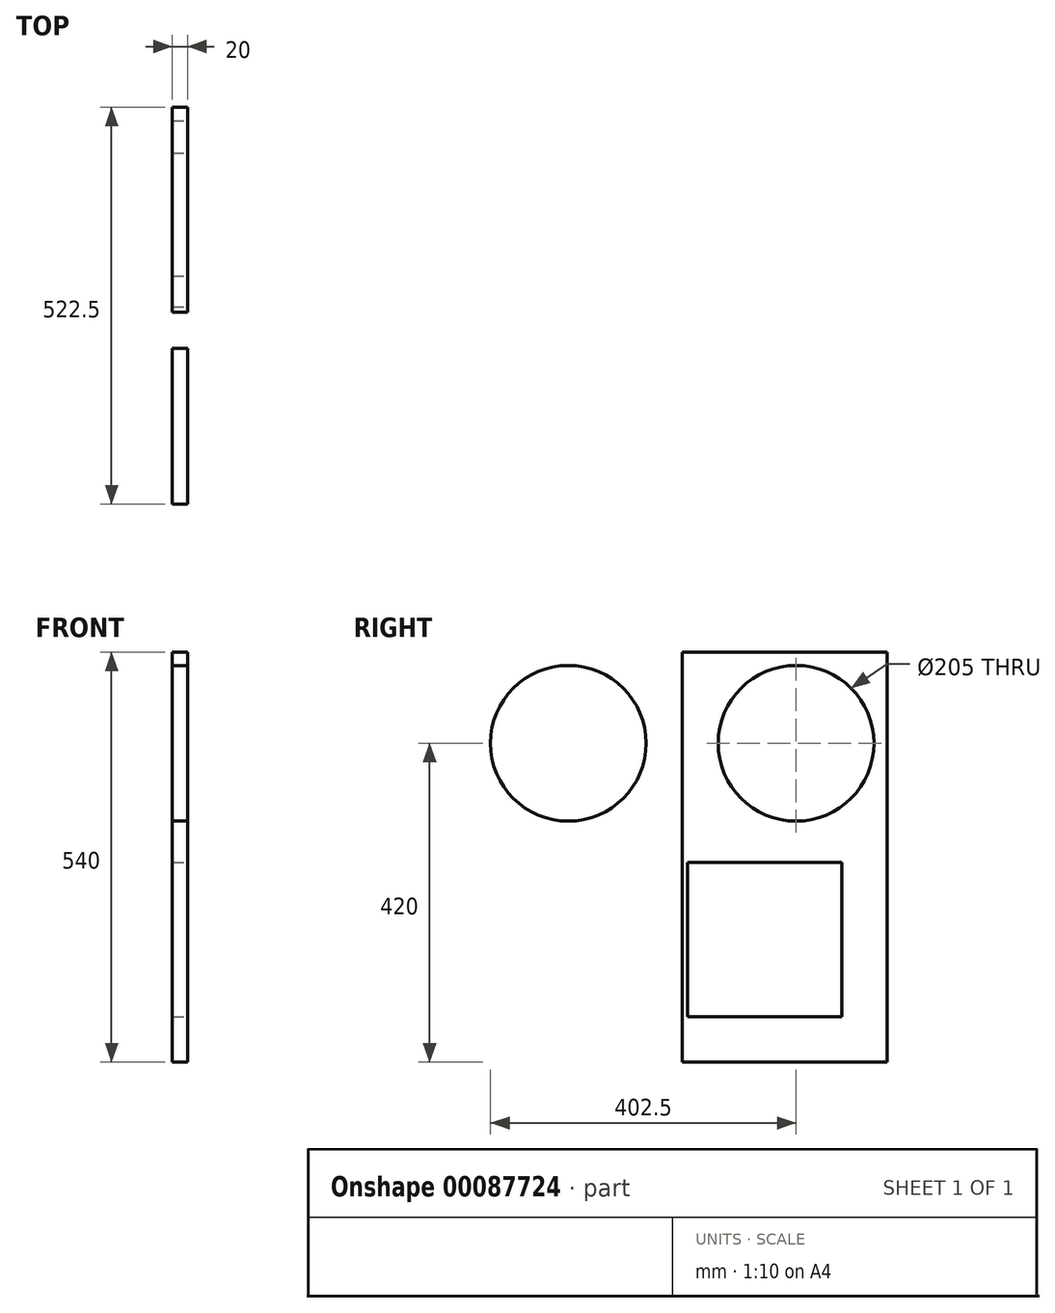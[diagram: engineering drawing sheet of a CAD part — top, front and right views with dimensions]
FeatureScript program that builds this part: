
annotation { "Feature Type Name" : "Feature", "Feature Type Description" : "" }
export const myFeature = defineFeature(function(context is Context, id is Id, definition is map)
    precondition{}
    {
        {
            var Q0;
            Q0=qCreatedBy(makeId("Right.planeOp"),FACE);
            var sketch = newSketch(context, id + "F0", { "sketchPlane" : qUnion([Q0])});
            skLineSegment(sketch, "E0.bottom", {"start": v(0, 0) * mm, "end": v(540, 0) * mm});
            skLineSegment(sketch, "E0.top", {"start": v(0, 540) * mm, "end": v(540, 540) * mm});
            skLineSegment(sketch, "E0.left", {"start": v(0, 0) * mm, "end": v(0, 540) * mm});
            skLineSegment(sketch, "E0.right", {"start": v(540, 0) * mm, "end": v(540, 540) * mm});
            skSolve(sketch);
        }
        {
            var Q0;
            Q0=makeQuery(id+"F0.imprint","IMPRINT",FACE,{"disambiguationData":[TD([[makeQuery(id+"F0.imprint","IMPRINT",EDGE,{"derivedFrom":sQuery(id+"F0.wireOp",EDGE,"E0.bottom")}),1.0]])]});
            extrude(context, id + "F1", {"entities" : qUnion([Q0]), "depth" : 20 * mm});
        }
        {
            var Q0;
            Q0=makeQuery(id+"F1.opExtrude","CAP_FACE",FACE,{"disambiguationData":[OSD([sQuery(id+"F0.wireOp",EDGE,"E0.bottom"),sQuery(id+"F0.wireOp",EDGE,"E0.top"),sQuery(id+"F0.wireOp",EDGE,"E0.left"),sQuery(id+"F0.wireOp",EDGE,"E0.right")])],"isStart":false});
            var sketch = newSketch(context, id + "F2", { "sketchPlane" : qUnion([Q0])});
            skLineSegment(sketch, "E1", {"start": v(540, 0) * mm, "end": v(540, 60) * mm});
            skLineSegment(sketch, "E2", {"start": v(540, 0) * mm, "end": v(480, 0) * mm});
            skLineSegment(sketch, "E3", {"start": v(480, 0) * mm, "end": v(480, 60) * mm});
            skLineSegment(sketch, "E4", {"start": v(480, 60) * mm, "end": v(540, 60) * mm});
            skLineSegment(sketch, "E5.bottom", {"start": v(480, 60) * mm, "end": v(277, 60) * mm});
            skLineSegment(sketch, "E5.top", {"start": v(480, 263) * mm, "end": v(277, 263) * mm});
            skLineSegment(sketch, "E5.left", {"start": v(480, 60) * mm, "end": v(480, 263) * mm});
            skLineSegment(sketch, "E5.right", {"start": v(277, 60) * mm, "end": v(277, 263) * mm});
            skLineSegment(sketch, "E6", {"start": v(540, 540) * mm, "end": v(540, 480) * mm});
            skLineSegment(sketch, "E7", {"start": v(540, 540) * mm, "end": v(480, 540) * mm});
            skLineSegment(sketch, "E8", {"start": v(480, 540) * mm, "end": v(480, 480) * mm});
            skLineSegment(sketch, "E9", {"start": v(480, 480) * mm, "end": v(540, 480) * mm});
            skLineSegment(sketch, "E10", {"start": v(480, 480) * mm, "end": v(480, 420) * mm});
            skLineSegment(sketch, "E11", {"start": v(480, 420) * mm, "end": v(420, 420) * mm});
            skCircle(sketch, "E12", {"center": v(420, 420) * mm, "radius": 102.5 * mm});
            skLineSegment(sketch, "E13", {"start": v(270, 540) * mm, "end": v(270, 0) * mm});
            skLineSegment(sketch, "E14.MirrorCS", {"start": v(0, 540) * mm, "end": v(0, 480) * mm});
            skCircle(sketch, "E15.MirrorC", {"center": v(120, 420) * mm, "radius": 102.5 * mm});
            skLineSegment(sketch, "E16.MirrorCS", {"start": v(60, 420) * mm, "end": v(120, 420) * mm});
            skLineSegment(sketch, "E17.MirrorCS", {"start": v(0, 540) * mm, "end": v(60, 540) * mm});
            skLineSegment(sketch, "E18.MirrorCS", {"start": v(60, 480) * mm, "end": v(60, 420) * mm});
            skLineSegment(sketch, "E19.MirrorCS", {"start": v(60, 540) * mm, "end": v(60, 480) * mm});
            skLineSegment(sketch, "E20.MirrorCS", {"start": v(60, 480) * mm, "end": v(0, 480) * mm});
            skSolve(sketch);
        }
        {
            var Q0;
            {var subQ0=sQuery(id+"F2.wireOp",EDGE,"E19.MirrorCS");var subQ1=sQuery(id+"F2.wireOp",EDGE,"E15.MirrorC");var subQ2=makeQuery(id+"F2.imprint","INTERSECT",VERTEX,{"derivedFrom":[subQ1,subQ0]});Q0=makeQuery(id+"F2.imprint","IMPRINT",FACE,{"disambiguationData":[TD([[makeQuery(id+"F2.imprint","IMPRINT",EDGE,{"disambiguationData":[TD([[subQ2,-1.0]])],"derivedFrom":subQ1}),-1.0]])]});}
            var Q1;
            {var subQ0=sQuery(id+"F2.wireOp",EDGE,"E19.MirrorCS");var subQ1=sQuery(id+"F2.wireOp",EDGE,"E15.MirrorC");var subQ2=makeQuery(id+"F2.imprint","INTERSECT",VERTEX,{"derivedFrom":[subQ1,subQ0]});Q1=makeQuery(id+"F2.imprint","IMPRINT",FACE,{"disambiguationData":[TD([[makeQuery(id+"F2.imprint","IMPRINT",EDGE,{"disambiguationData":[TD([[subQ2,1.0]])],"derivedFrom":subQ1}),-1.0]])]});}
            var Q2;
            {var subQ0=sQuery(id+"F2.wireOp",EDGE,"E9");var subQ1=sQuery(id+"F2.wireOp",EDGE,"E8");var subQ2=makeQuery(id+"F2.imprint","INTERSECT",VERTEX,{"derivedFrom":[subQ1,subQ0]});Q2=makeQuery(id+"F2.imprint","IMPRINT",FACE,{"disambiguationData":[TD([[makeQuery(id+"F2.imprint","IMPRINT",EDGE,{"disambiguationData":[TD([[subQ2,1.0]])],"derivedFrom":subQ1}),-1.0]])]});}
            var Q3;
            {var subQ0=sQuery(id+"F2.wireOp",EDGE,"E9");var subQ1=sQuery(id+"F2.wireOp",EDGE,"E8");var subQ2=makeQuery(id+"F2.imprint","INTERSECT",VERTEX,{"derivedFrom":[subQ1,subQ0]});Q3=makeQuery(id+"F2.imprint","IMPRINT",FACE,{"disambiguationData":[TD([[makeQuery(id+"F2.imprint","IMPRINT",EDGE,{"disambiguationData":[TD([[subQ2,1.0]])],"derivedFrom":subQ1}),1.0]])]});}
            var Q4;
            Q4=makeQuery(id+"F2.imprint","IMPRINT",FACE,{"disambiguationData":[TD([[makeQuery(id+"F2.imprint","IMPRINT",EDGE,{"derivedFrom":sQuery(id+"F2.wireOp",EDGE,"E5.bottom")}),-1.0]])]});
            extrude(context, id + "F3", {"entities" : qUnion([Q0, Q1, Q2, Q3, Q4]), "operationType" : NewBodyOperationType.REMOVE, "oppositeDirection" : true, "depth" : 25 * mm});
        }
    });
